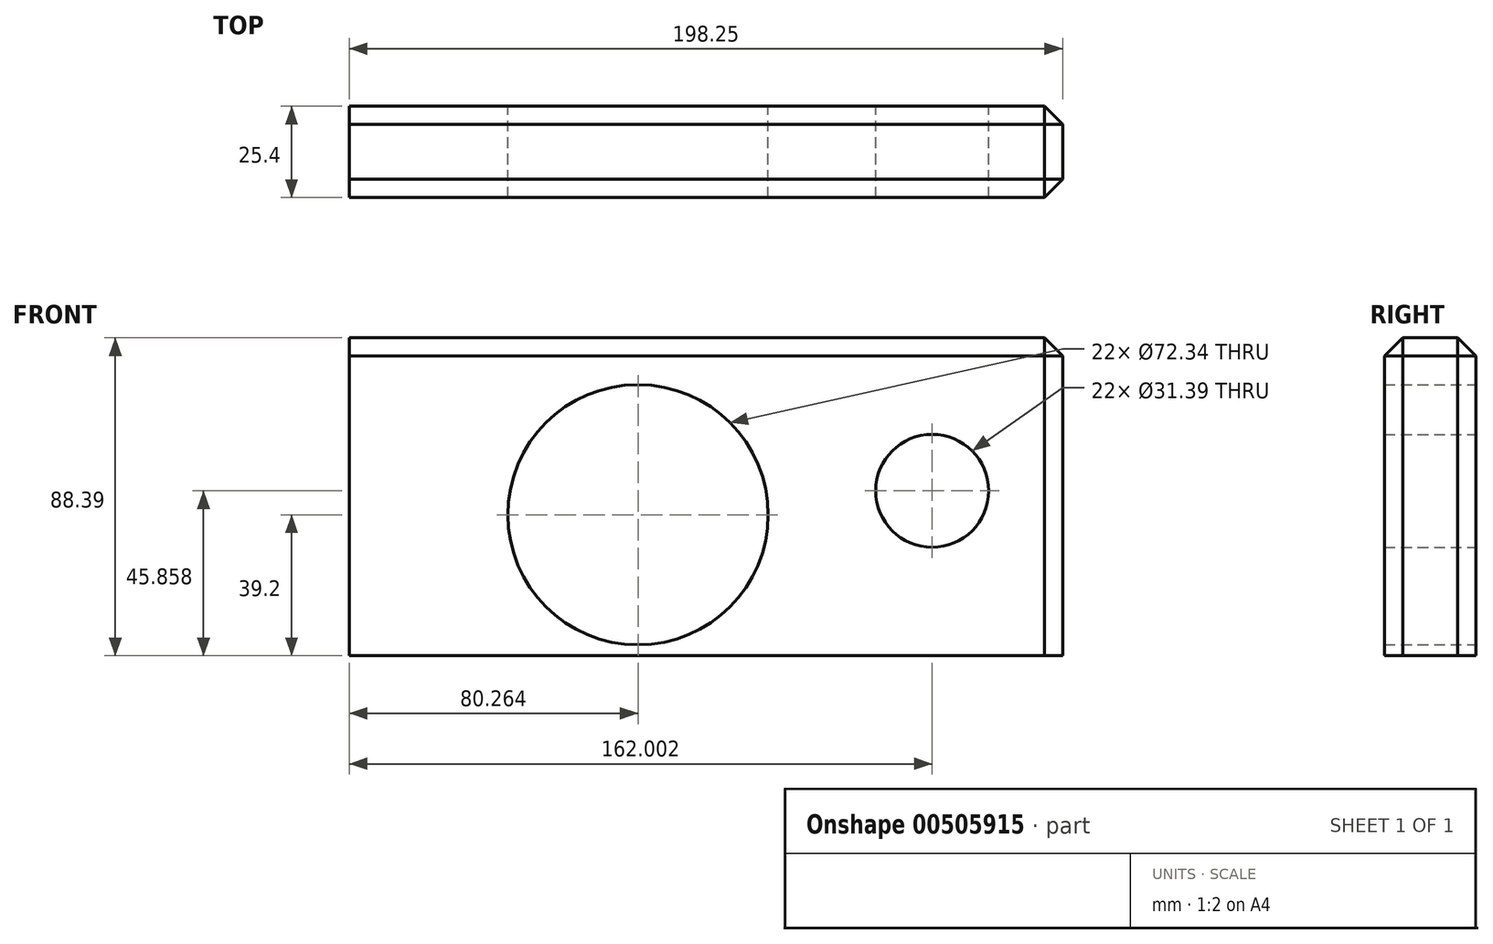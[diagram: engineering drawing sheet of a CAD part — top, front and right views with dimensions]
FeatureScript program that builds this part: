
annotation { "Feature Type Name" : "Feature", "Feature Type Description" : "" }
export const myFeature = defineFeature(function(context is Context, id is Id, definition is map)
    precondition{}
    {
        {
            var Q0;
            Q0=qCreatedBy(makeId("Front.planeOp"),FACE);
            var sketch = newSketch(context, id + "F0", { "sketchPlane" : qUnion([Q0])});
            skLineSegment(sketch, "E0.bottom", {"start": v(-89.88, 36.06) * mm, "end": v(108.37, 36.06) * mm});
            skLineSegment(sketch, "E0.top", {"start": v(-89.88, -52.33) * mm, "end": v(108.37, -52.33) * mm});
            skLineSegment(sketch, "E0.left", {"start": v(-89.88, 36.06) * mm, "end": v(-89.88, -52.33) * mm});
            skLineSegment(sketch, "E0.right", {"start": v(108.37, 36.06) * mm, "end": v(108.37, -52.33) * mm});
            skCircle(sketch, "E1", {"center": v(-9.62, -13.13) * mm, "radius": 36.17 * mm});
            skCircle(sketch, "E2", {"center": v(72.12, -6.47) * mm, "radius": 15.7 * mm});
            skSolve(sketch);
        }
        {
            var Q0;
            Q0=makeQuery(id+"F0.imprint","IMPRINT",FACE,{"disambiguationData":[TD([[makeQuery(id+"F0.imprint","IMPRINT",EDGE,{"derivedFrom":sQuery(id+"F0.wireOp",EDGE,"E0.bottom")}),-1.0]])]});
            extrude(context, id + "F1", {"entities" : qUnion([Q0]), "depth" : 25.4 * mm});
        }
        {
            var Q0;
            Q0=makeQuery(id+"F1.opExtrude","SWEPT_EDGE",EDGE,{"disambiguationData":[OSD([sQuery(id+"F0.wireOp",EDGE,"E0.bottom"),sQuery(id+"F0.wireOp",EDGE,"E0.right")])]});
            var Q1;
            Q1=makeQuery(id+"F1.opExtrude","CAP_EDGE",EDGE,{"disambiguationData":[OSD([sQuery(id+"F0.wireOp",EDGE,"E0.right")])],"isStart":false});
            var Q2;
            Q2=makeQuery(id+"F1.opExtrude","CAP_EDGE",EDGE,{"disambiguationData":[OSD([sQuery(id+"F0.wireOp",EDGE,"E0.bottom")])],"isStart":false});
            var Q3;
            Q3=makeQuery(id+"F1.opExtrude","CAP_EDGE",EDGE,{"disambiguationData":[OSD([sQuery(id+"F0.wireOp",EDGE,"E0.right")])],"isStart":true});
            var Q4;
            Q4=makeQuery(id+"F1.opExtrude","CAP_EDGE",EDGE,{"disambiguationData":[OSD([sQuery(id+"F0.wireOp",EDGE,"E0.bottom")])],"isStart":true});
            chamfer(context, id + "F2", {"entities" : qUnion([Q0, Q1, Q2, Q3, Q4]), "width" : 5.08 * mm, "tangentPropagation" : true});
        }
    });
